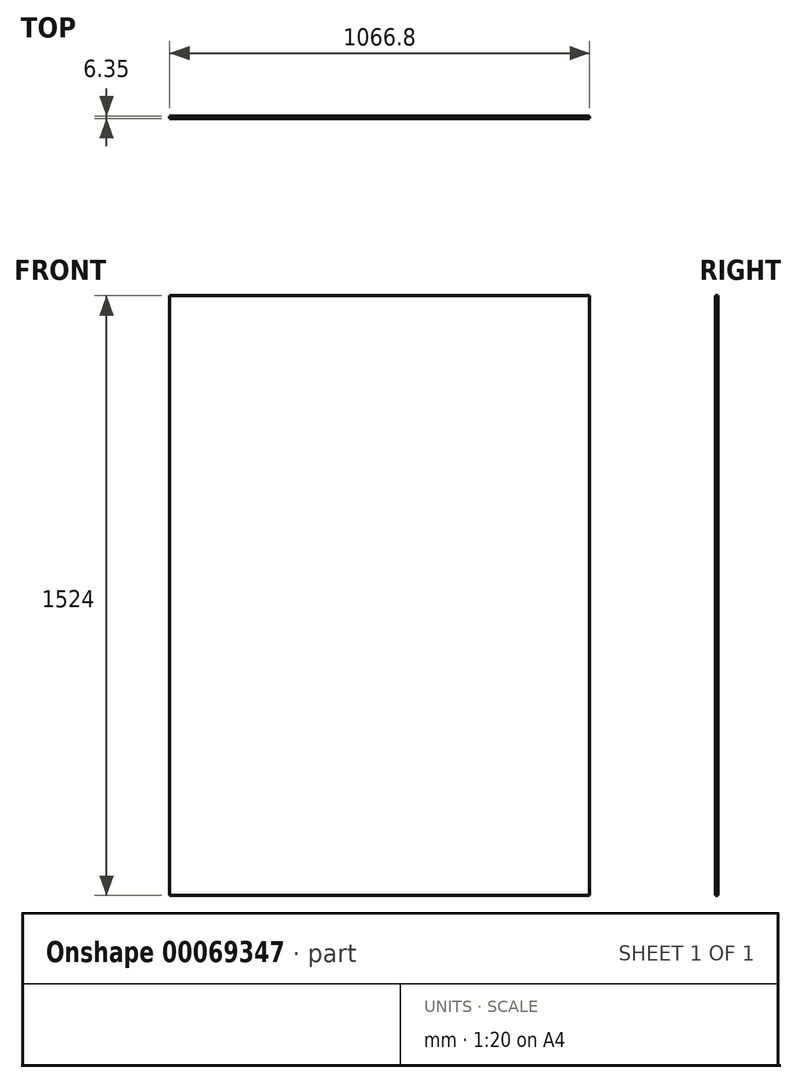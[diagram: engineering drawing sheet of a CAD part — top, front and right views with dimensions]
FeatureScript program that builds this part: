
annotation { "Feature Type Name" : "Feature", "Feature Type Description" : "" }
export const myFeature = defineFeature(function(context is Context, id is Id, definition is map)
    precondition{}
    {
        {
            var Q0;
            Q0=qCreatedBy(makeId("Front.planeOp"),FACE);
            var sketch = newSketch(context, id + "F0", { "sketchPlane" : qUnion([Q0])});
            skLineSegment(sketch, "E0.bottom", {"start": v(-536.34, 915.61) * mm, "end": v(530.46, 915.61) * mm});
            skLineSegment(sketch, "E0.top", {"start": v(-536.34, -608.39) * mm, "end": v(530.46, -608.39) * mm});
            skLineSegment(sketch, "E0.left", {"start": v(-536.34, 915.61) * mm, "end": v(-536.34, -608.39) * mm});
            skLineSegment(sketch, "E0.right", {"start": v(530.46, 915.61) * mm, "end": v(530.46, -608.39) * mm});
            skSolve(sketch);
        }
        {
            var Q0;
            Q0=qSketchRegion(id+"F0",true);
            extrude(context, id + "F1", {"entities" : qUnion([Q0]), "depth" : 6.35 * mm});
        }
    });
